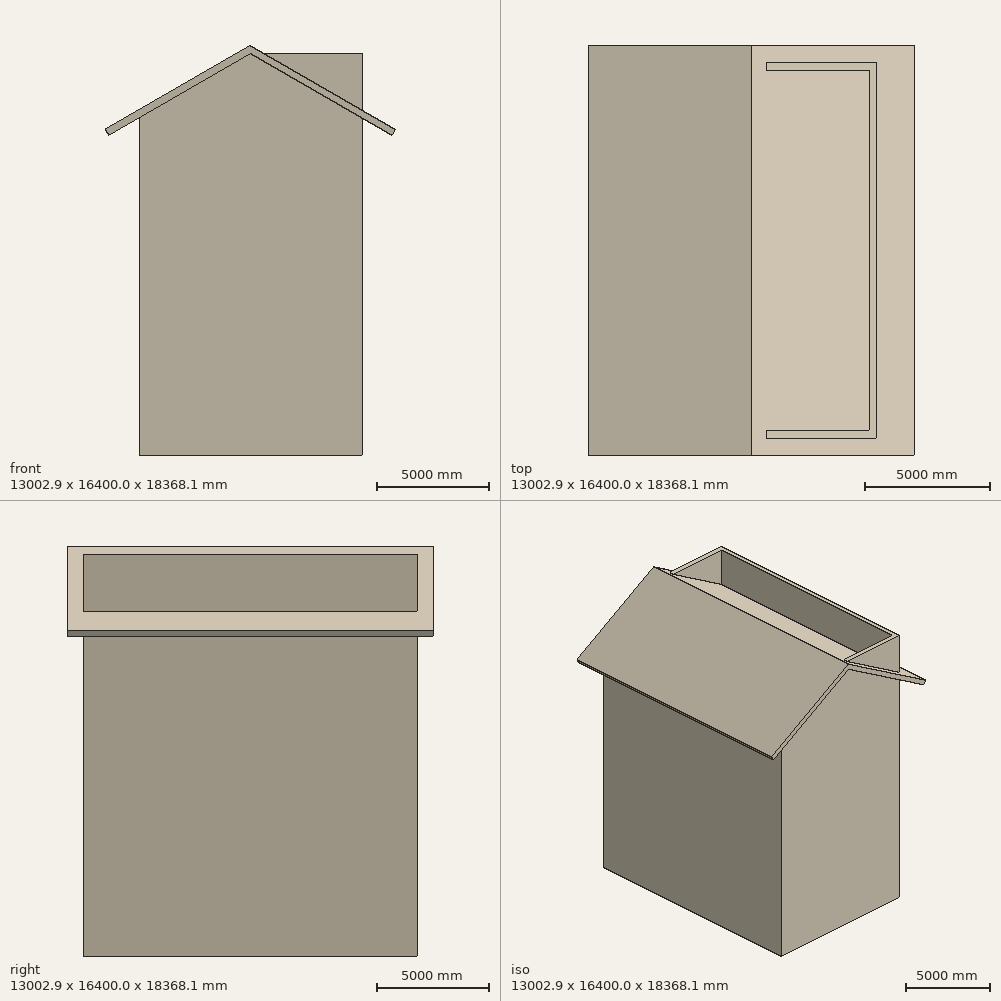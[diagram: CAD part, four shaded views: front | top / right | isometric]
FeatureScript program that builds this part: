
annotation { "Feature Type Name" : "Feature", "Feature Type Description" : "" }
export const myFeature = defineFeature(function(context is Context, id is Id, definition is map)
    precondition{}
    {
        {
            var Q0;
            Q0=qCreatedBy(makeId("Top.planeOp"),FACE);
            var sketch = newSketch(context, id + "F0", { "sketchPlane" : qUnion([Q0])});
            skLineSegment(sketch, "E0.top", {"start": v(-5000, 7500) * mm, "end": v(5000, 7500) * mm});
            skLineSegment(sketch, "E0.left", {"start": v(-5000, -7500) * mm, "end": v(-5000, 7500) * mm});
            skLineSegment(sketch, "E1", {"start": v(5000, 7500) * mm, "end": v(5000, -7500) * mm});
            skLineSegment(sketch, "E2", {"start": v(5000, -7500) * mm, "end": v(-5000, -7500) * mm});
            skLineSegment(sketch, "E3", {"start": v(-5000, 7500) * mm, "end": v(5000, -7500) * mm, "construction": true});
            skLineSegment(sketch, "E4.bottom", {"start": v(4700, 7200) * mm, "end": v(-4700, 7200) * mm});
            skLineSegment(sketch, "E4.top", {"start": v(4700, -7200) * mm, "end": v(-4700, -7200) * mm});
            skLineSegment(sketch, "E4.left", {"start": v(4700, 7200) * mm, "end": v(4700, -7200) * mm});
            skLineSegment(sketch, "E4.right", {"start": v(-4700, 7200) * mm, "end": v(-4700, -7200) * mm});
            skLineSegment(sketch, "E5", {"start": v(4700, 7200) * mm, "end": v(-4700, -7200) * mm, "construction": true});
            skSolve(sketch);
        }
        {
            var Q0;
            Q0 = qSketchRegion(id + "F0", true);
            extrude(context, id + "F1", {"entities" : qUnion([Q0]), "depth" : 18000 * mm, "offsetDistance" : 25 * mm});
        }
        {
            var Q0;
            Q0=makeQuery(id+"F1.opExtrude","SWEPT_FACE",FACE,{"disambiguationData":[OSD([sQuery(id+"F0.wireOp",EDGE,"E2")])]});
            var sketch = newSketch(context, id + "F2", { "sketchPlane" : qUnion([Q0])});
            skLineSegment(sketch, "E6", {"start": v(0, 18000) * mm, "end": v(-5000, 15113.25) * mm});
            skLineSegment(sketch, "E7", {"start": v(-5000, 15113.25) * mm, "end": v(-5000, 18000) * mm});
            skLineSegment(sketch, "E8", {"start": v(-5000, 18000) * mm, "end": v(0, 18000) * mm});
            skLineSegment(sketch, "E9", {"start": v(0, 18000) * mm, "end": v(5000, 15113.25) * mm});
            skLineSegment(sketch, "E10", {"start": v(5000, 15113.25) * mm, "end": v(0, 18000) * mm});
            skLineSegment(sketch, "E11", {"start": v(-5000, 15113.25) * mm, "end": v(5000, 15113.25) * mm, "construction": true});
            skSolve(sketch);
        }
        {
            var Q0;
            Q0 = qSketchRegion(id + "F2", true);
            var Q1;
            {var subQ0=sQuery(id+"F2.wireOp",EDGE,"E10");Q1=makeQuery(id+"F2.imprint","IMPRINT",FACE,{"disambiguationData":[TD([[makeQuery(id+"F2.imprint","IMPRINT",EDGE,{"derivedFrom":subQ0}),-1.0]])]});}
            extrude(context, id + "F3", {"entities" : qUnion([Q0, Q1]), "operationType" : NewBodyOperationType.REMOVE, "oppositeDirection" : true, "depth" : 15000 * mm, "offsetDistance" : 25 * mm});
        }
        {
            var Q0;
            Q0=qCreatedBy(makeId("Front.planeOp"),FACE);
            var sketch = newSketch(context, id + "F4", { "sketchPlane" : qUnion([Q0])});
            skLineSegment(sketch, "E12", {"start": v(-6345.2, 14336.6) * mm, "end": v(-6495.2, 14596.41) * mm});
            skLineSegment(sketch, "E13", {"start": v(-6495.2, 14596.41) * mm, "end": v(0, 18346.41) * mm});
            skLineSegment(sketch, "E14", {"start": v(0, 18346.41) * mm, "end": v(6495.2, 14596.41) * mm});
            skLineSegment(sketch, "E15", {"start": v(6345.2, 14336.6) * mm, "end": v(6495.2, 14596.41) * mm});
            skLineSegment(sketch, "E16", {"start": v(6345.2, 14336.6) * mm, "end": v(0, 18000) * mm});
            skLineSegment(sketch, "E17", {"start": v(0, 18000) * mm, "end": v(-6345.2, 14336.6) * mm});
            skSolve(sketch);
        }
        {
            var Q0;
            Q0 = qSketchRegion(id + "F4", true);
            extrude(context, id + "F5", {"entities" : qUnion([Q0]), "operationType" : NewBodyOperationType.ADD, "depth" : 8200 * mm, "offsetDistance" : 25 * mm, "hasSecondDirection" : true, "secondDirectionOppositeDirection" : true, "secondDirectionDepth" : 8200 * mm});
        }
        {
            var Q0;
            Q0=makeQuery(id+"F5.opExtrude","SWEPT_FACE",FACE,{"disambiguationData":[OSD([sQuery(id+"F4.wireOp",EDGE,"E13")])]});
            var sketch = newSketch(context, id + "F6", { "sketchPlane" : qUnion([Q0])});
            skLineSegment(sketch, "E18.bottom", {"start": v(2277.31, 3073.02) * mm, "end": v(8521.41, 3073.02) * mm});
            skLineSegment(sketch, "E18.top", {"start": v(2277.31, -500.66) * mm, "end": v(8521.41, -500.66) * mm});
            skLineSegment(sketch, "E18.left", {"start": v(2277.31, 3073.02) * mm, "end": v(2277.31, -500.66) * mm});
            skLineSegment(sketch, "E18.right", {"start": v(8521.41, 3073.02) * mm, "end": v(8521.41, -500.66) * mm});
            skSolve(sketch);
        }
        {
            var Q0;
            Q0 = qSketchRegion(id + "F6", true);
            var Q1;
            Q1=makeQuery(id+"F6.imprint","IMPRINT",FACE,{"disambiguationData":[TD([[makeQuery(id+"F6.imprint","IMPRINT",EDGE,{"derivedFrom":sQuery(id+"F6.wireOp",EDGE,"E18.bottom")}),1.0]])]});
            extrude(context, id + "F7", {"entities" : qUnion([Q0, Q1]), "operationType" : NewBodyOperationType.ADD, "depth" : 25 * mm, "offsetDistance" : 25 * mm});
        }
    });
